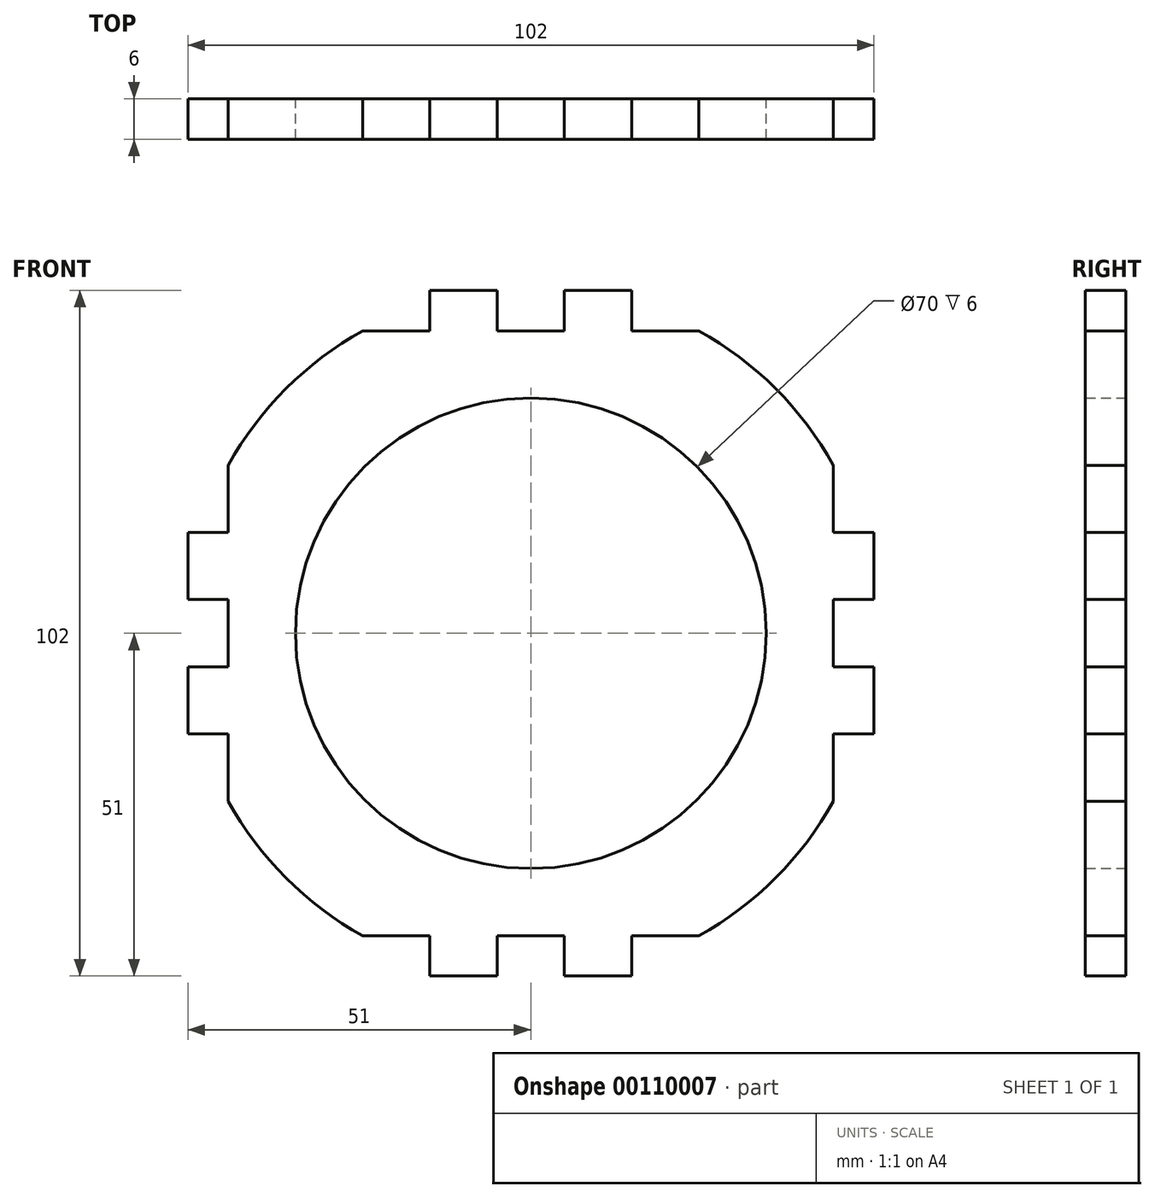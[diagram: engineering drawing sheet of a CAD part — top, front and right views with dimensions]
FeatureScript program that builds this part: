
annotation { "Feature Type Name" : "Feature", "Feature Type Description" : "" }
export const myFeature = defineFeature(function(context is Context, id is Id, definition is map)
    precondition{}
    {
        {
            var Q0;
            Q0=qCreatedBy(makeId("Front.planeOp"),FACE);
            var sketch = newSketch(context, id + "F0", { "sketchPlane" : qUnion([Q0])});
            skLineSegment(sketch, "E0.bottom", {"start": v(25, -45) * mm, "end": v(15, -45) * mm});
            skLineSegment(sketch, "E0.top", {"start": v(25, 45) * mm, "end": v(15, 45) * mm});
            skLineSegment(sketch, "E0.left", {"start": v(45, -25) * mm, "end": v(45, -15) * mm});
            skLineSegment(sketch, "E0.right", {"start": v(-45, -25) * mm, "end": v(-45, -15) * mm});
            skPoint(sketch, "E0.middle", {"position": v(0, 0) * mm});
            skArc(sketch, "E1", {"start": v(-45, -25) * mm, "mid": v(-36.4, -36.4) * mm, "end": v(-25, -45) * mm});
            skPoint(sketch, "E2", {"position": v(-45, 25) * mm});
            skPoint(sketch, "E3", {"position": v(-45, -25) * mm});
            skArc(sketch, "E4.trimOffspring", {"start": v(45, 25) * mm, "mid": v(36.4, 36.4) * mm, "end": v(25, 45) * mm});
            skArc(sketch, "E5.trimOffspring", {"start": v(-25, 45) * mm, "mid": v(-36.4, 36.4) * mm, "end": v(-45, 25) * mm});
            skArc(sketch, "E6.trimOffspring", {"start": v(25, -45) * mm, "mid": v(36.4, -36.4) * mm, "end": v(45, -25) * mm});
            skPoint(sketch, "E7.orphan", {"position": v(-45, -45) * mm});
            skPoint(sketch, "E8.orphan", {"position": v(45, -45) * mm});
            skPoint(sketch, "E9.orphan", {"position": v(45, 45) * mm});
            skPoint(sketch, "E10.orphan", {"position": v(-45, 45) * mm});
            skLineSegment(sketch, "E11.bottom", {"start": v(-51, 15) * mm, "end": v(-45, 15) * mm});
            skLineSegment(sketch, "E11.top", {"start": v(-51, 5) * mm, "end": v(-45, 5) * mm});
            skLineSegment(sketch, "E11.right", {"start": v(-51, 15) * mm, "end": v(-51, 5) * mm});
            skLineSegment(sketch, "E12.top", {"start": v(-15, 51) * mm, "end": v(-5, 51) * mm});
            skLineSegment(sketch, "E12.left", {"start": v(-15, 51) * mm, "end": v(-15, 45) * mm});
            skLineSegment(sketch, "E12.right", {"start": v(-5, 51) * mm, "end": v(-5, 45) * mm});
            skLineSegment(sketch, "E13.trimOffspring", {"start": v(-45, 15) * mm, "end": v(-45, 25) * mm});
            skLineSegment(sketch, "E14.trimOffspring", {"start": v(-15, 45) * mm, "end": v(-25, 45) * mm});
            skLineSegment(sketch, "E15.MirrorCS", {"start": v(15, 51) * mm, "end": v(5, 51) * mm});
            skLineSegment(sketch, "E16.MirrorCS", {"start": v(15, 51) * mm, "end": v(15, 45) * mm});
            skLineSegment(sketch, "E17.MirrorCS", {"start": v(5, 51) * mm, "end": v(5, 45) * mm});
            skLineSegment(sketch, "E18.MirrorCS", {"start": v(51, 15) * mm, "end": v(45, 15) * mm});
            skLineSegment(sketch, "E19.MirrorCS", {"start": v(51, 5) * mm, "end": v(45, 5) * mm});
            skLineSegment(sketch, "E20.MirrorCS", {"start": v(51, 15) * mm, "end": v(51, 5) * mm});
            skLineSegment(sketch, "E21.trimOffspring", {"start": v(5, 45) * mm, "end": v(-5, 45) * mm});
            skLineSegment(sketch, "E22.trimOffspring", {"start": v(45, 15) * mm, "end": v(45, 25) * mm});
            skLineSegment(sketch, "E23.MirrorCS", {"start": v(51, -5) * mm, "end": v(45, -5) * mm});
            skLineSegment(sketch, "E24.MirrorCS", {"start": v(-51, -15) * mm, "end": v(-45, -15) * mm});
            skLineSegment(sketch, "E25.MirrorCS", {"start": v(51, -15) * mm, "end": v(45, -15) * mm});
            skLineSegment(sketch, "E26.MirrorCS", {"start": v(-51, -5) * mm, "end": v(-45, -5) * mm});
            skLineSegment(sketch, "E27.MirrorCS", {"start": v(51, -15) * mm, "end": v(51, -5) * mm});
            skLineSegment(sketch, "E28.MirrorCS", {"start": v(-51, -15) * mm, "end": v(-51, -5) * mm});
            skLineSegment(sketch, "E29.MirrorCS", {"start": v(5, -51) * mm, "end": v(5, -45) * mm});
            skLineSegment(sketch, "E30.MirrorCS", {"start": v(15, -51) * mm, "end": v(15, -45) * mm});
            skLineSegment(sketch, "E31.MirrorCS", {"start": v(-15, -51) * mm, "end": v(-15, -45) * mm});
            skLineSegment(sketch, "E32.MirrorCS", {"start": v(-5, -51) * mm, "end": v(-5, -45) * mm});
            skLineSegment(sketch, "E33.MirrorCS", {"start": v(15, -51) * mm, "end": v(5, -51) * mm});
            skLineSegment(sketch, "E34.MirrorCS", {"start": v(-15, -51) * mm, "end": v(-5, -51) * mm});
            skLineSegment(sketch, "E35.trimOffspring", {"start": v(-45, -5) * mm, "end": v(-45, 5) * mm});
            skLineSegment(sketch, "E36.trimOffspring", {"start": v(45, -5) * mm, "end": v(45, 5) * mm});
            skLineSegment(sketch, "E37.trimOffspring", {"start": v(-15, -45) * mm, "end": v(-25, -45) * mm});
            skLineSegment(sketch, "E38.trimOffspring", {"start": v(5, -45) * mm, "end": v(-5, -45) * mm});
            skCircle(sketch, "E39", {"center": v(0, 0) * mm, "radius": 35 * mm});
            skSolve(sketch);
        }
        {
            var Q0;
            Q0 = qSketchRegion(id + "F0", true);
            extrude(context, id + "F1", {"entities" : qUnion([Q0]), "depth" : 6 * mm});
        }
    });
